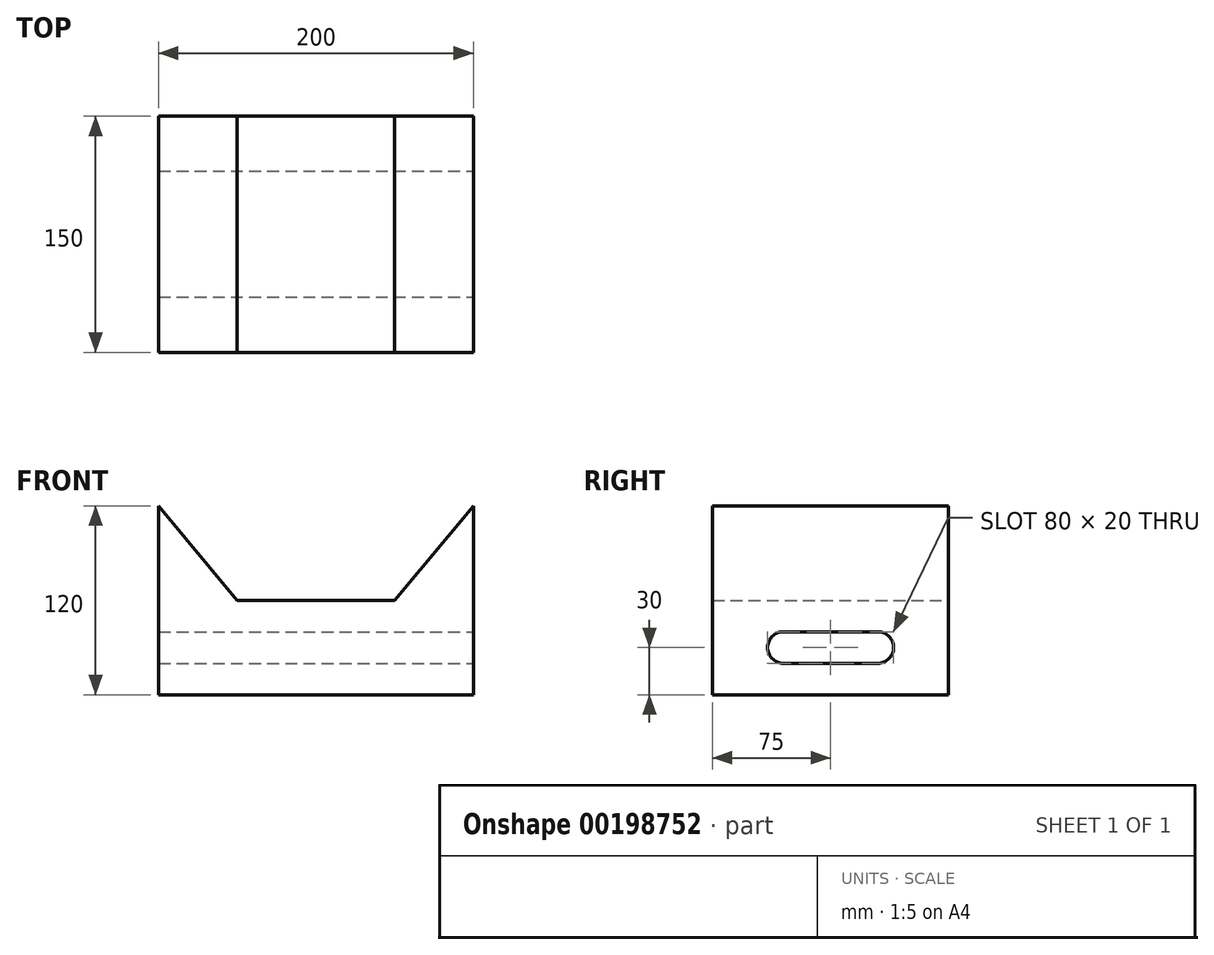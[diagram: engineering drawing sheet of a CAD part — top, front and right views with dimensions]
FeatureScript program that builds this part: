
annotation { "Feature Type Name" : "Feature", "Feature Type Description" : "" }
export const myFeature = defineFeature(function(context is Context, id is Id, definition is map)
    precondition{}
    {
        {
            var Q0;
            Q0=qCreatedBy(makeId("Front.planeOp"),FACE);
            var sketch = newSketch(context, id + "F0", { "sketchPlane" : qUnion([Q0])});
            skLineSegment(sketch, "E0.top", {"start": v(100, -60) * mm, "end": v(-100, -60) * mm});
            skLineSegment(sketch, "E0.left", {"start": v(100, 60) * mm, "end": v(100, -60) * mm});
            skLineSegment(sketch, "E0.right", {"start": v(-100, 60) * mm, "end": v(-100, -60) * mm});
            skPoint(sketch, "E0.middle", {"position": v(0, 0) * mm});
            skLineSegment(sketch, "E1", {"start": v(-100, 60) * mm, "end": v(-50, 0) * mm});
            skPoint(sketch, "E1.endSnap0", {"position": v(-100, 0) * mm});
            skLineSegment(sketch, "E2", {"start": v(-50, 0) * mm, "end": v(50, 0) * mm});
            skPoint(sketch, "E2.endSnap0", {"position": v(100, 0) * mm});
            skLineSegment(sketch, "E3", {"start": v(50, 0) * mm, "end": v(100, 60) * mm});
            skSolve(sketch);
        }
        {
            var Q0;
            Q0 = qSketchRegion(id + "F0", true);
            extrude(context, id + "F1", {"entities" : qUnion([Q0]), "endBound" : BoundingType.SYMMETRIC, "depth" : 150 * mm});
        }
        {
            var Q0;
            Q0=makeQuery(id+"F1.opExtrude","SWEPT_FACE",FACE,{"disambiguationData":[OSD([sQuery(id+"F0.wireOp",EDGE,"E0.left")])]});
            var sketch = newSketch(context, id + "F2", { "sketchPlane" : qUnion([Q0])});
            skLineSegment(sketch, "E4.bottom", {"start": v(30, -20) * mm, "end": v(-30, -20) * mm});
            skLineSegment(sketch, "E4.top", {"start": v(30, -40) * mm, "end": v(-30, -40) * mm});
            skLineSegment(sketch, "E4.left", {"start": v(30, -20) * mm, "end": v(30, -40) * mm});
            skLineSegment(sketch, "E4.right", {"start": v(-30, -20) * mm, "end": v(-30, -40) * mm});
            skPoint(sketch, "E4.middle", {"position": v(0, -30) * mm});
            skCircle(sketch, "E5", {"center": v(30, -30) * mm, "radius": 10 * mm});
            skCircle(sketch, "E6", {"center": v(-30, -30) * mm, "radius": 10 * mm});
            skSolve(sketch);
        }
        {
            var Q0;
            Q0 = qSketchRegion(id + "F2", true);
            extrude(context, id + "F3", {"entities" : qUnion([Q0]), "operationType" : NewBodyOperationType.REMOVE, "endBound" : BoundingType.THROUGH_ALL, "oppositeDirection" : true, "depth" : 25 * mm});
        }
    });
